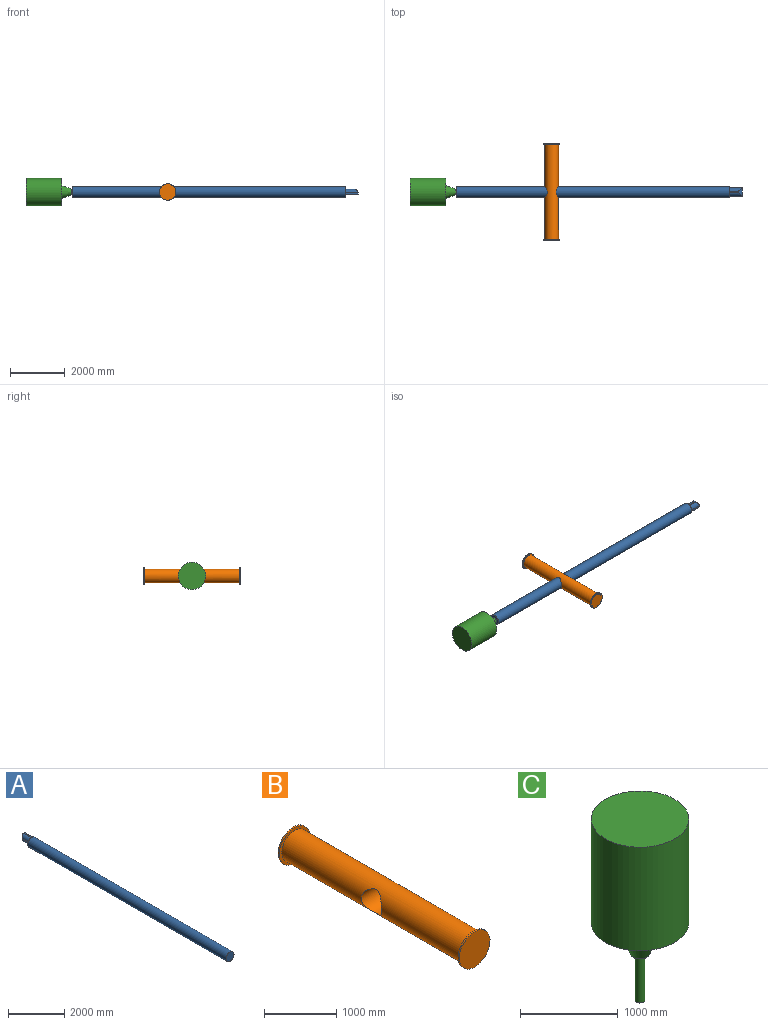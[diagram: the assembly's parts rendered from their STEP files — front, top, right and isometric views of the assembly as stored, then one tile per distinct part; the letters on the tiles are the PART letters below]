
ASSEMBLY  parts=3 mates=2
PART A: 22 faces, bbox 400x10464.2x400 mm
  f0: plane 464.16x294.29mm, normal (1,0,0), area 3044mm2, adj f3,f4,f5,f7,f15,f16,f18
  f1: cylinder r=200mm len=10000mm, axis (0,1,0), area 12566370.6mm2, adj f2,f3
  f2: plane 400x400mm, normal (0,-1,0), area 125663.7mm2, adj f1
  f3: plane 400x400mm, normal (0,1,0), area 74372.8mm2, adj f0,f1,f4,f5,f6,f8,f10,f11
  f4: plane 464.16x67.22mm, normal (0,0,1), area 31200.2mm2, adj f0,f3,f7,f10
  f5: plane 464.16x67.22mm, normal (0,0,-1), area 31200.2mm2, adj f0,f3,f7,f8
  f6: plane 331.38x28.73mm, normal (-1,0,0), area 9519.6mm2, adj f3,f8,f9,f10
  f7: plane 294.29x67.22mm, normal (0,1,0), area 19781.7mm2, adj f0,f4,f5,f9
  f8: cylinder r=132.78mm len=464.16mm, axis (0,1,0), area 86748mm2, adj f3,f5,f6,f9
  f9: cylinder r=132.78mm len=294.29mm, axis (0,0,1), area 41253.7mm2, adj f6,f7,f8,f10
  f10: cylinder r=132.78mm len=464.16mm, axis (0,-1,0), area 86748mm2, adj f3,f4,f6,f9
  f11: plane 289.29x2.5mm, normal (-1,0,0), area 723.2mm2, adj f3,f14,f15,f16
  f12: cylinder r=197.5mm len=9995mm, axis (0,1,0), area 12403086.3mm2, adj f13,f14
  f13: plane 395x395mm, normal (0,1,0), area 122541.7mm2, adj f12
  f14: plane 395x395mm, normal (0,-1,0), area 72691.8mm2, adj f11,f12,f15,f16,f17,f19,f21
  f15: plane 464.16x67.22mm, normal (0,0,-1), area 31200.2mm2, adj f0,f11,f14,f18,f21
  f16: plane 464.16x67.22mm, normal (0,0,1), area 31200.2mm2, adj f0,f11,f14,f18,f19
  f17: plane 333.88x28.73mm, normal (1,0,0), area 9591.5mm2, adj f14,f19,f20,f21
  f18: plane 289.29x67.22mm, normal (0,-1,0), area 19445.6mm2, adj f0,f15,f16,f20
  f19: cylinder r=130.28mm len=464.16mm, axis (0,1,0), area 85300.6mm2, adj f14,f16,f17,f20
  f20: cylinder r=130.28mm len=289.29mm, axis (0,0,1), area 39825.6mm2, adj f17,f18,f19,f21
  f21: cylinder r=130.28mm len=464.16mm, axis (0,-1,0), area 85300.6mm2, adj f14,f15,f17,f20
PART B: 8 faces, bbox 600x3550x600 mm
  f0: cylinder r=300mm len=600mm, axis (0,-1,0), area 47123.9mm2, adj f1,f2
  f1: plane 600x600mm, normal (0,1,0), area 86393.8mm2, adj f0,f3
  f2: plane 600x600mm, normal (0,-1,0), area 282743.3mm2, adj f0
  f3: cylinder r=250mm len=3500mm, axis (0,1,0), area 5218814.1mm2, adj f1,f5,f7
  f4: cylinder r=300mm len=600mm, axis (0,1,0), area 47123.9mm2, adj f5,f6
  f5: plane 600x600mm, normal (0,-1,0), area 86393.8mm2, adj f3,f4
  f6: plane 600x600mm, normal (0,1,0), area 282743.3mm2, adj f4
  f7: cylinder r=200mm len=500.01mm, axis (1,0,0), area 510553.1mm2, adj f3
PART C: 8 faces, bbox 1000x1000x2274 mm
  f0: cone r=238.85mm half-angle=20deg, axis (0,0,1), area 432161.4mm2, adj f3,f4
  f1: cylinder r=500mm len=1300mm, axis (0,0,-1), area 4084070.4mm2, adj f2,f3
  f2: plane 1000x1000mm, normal (0,0,1), area 785398.2mm2, adj f1
  f3: plane 1000x1000mm, normal (0,0,-1), area 606174.3mm2, adj f0,f1
  f4: cylinder r=100mm len=200mm, axis (0,0,1), area 1581mm2, adj f0,f5
  f5: plane 200x200mm, normal (0,0,-1), area 23561.9mm2, adj f4,f6
  f6: cylinder r=50mm len=590mm, axis (0,0,1), area 185354mm2, adj f5,f7
  f7: plane 100x100mm, normal (0,0,-1), area 7854mm2, adj f6
PLACE A rot(axis=(0.58,0.58,-0.58),120deg) t=(5216.57,-515.97,337.53)mm
PLACE B t=(-1283.43,-515.97,337.53)mm
PLACE C rot(axis=(0.71,0,-0.71),180deg) t=(-5167.43,-515.97,337.53)mm
MATE fastened C.f4 <-> A.f1  axis (1,0,0) through (-4783.43,-515.97,337.53)mm
MATE fastened A.f1 <-> B.f7  axis (1,0,0) through (216.57,-515.97,337.53)mm
